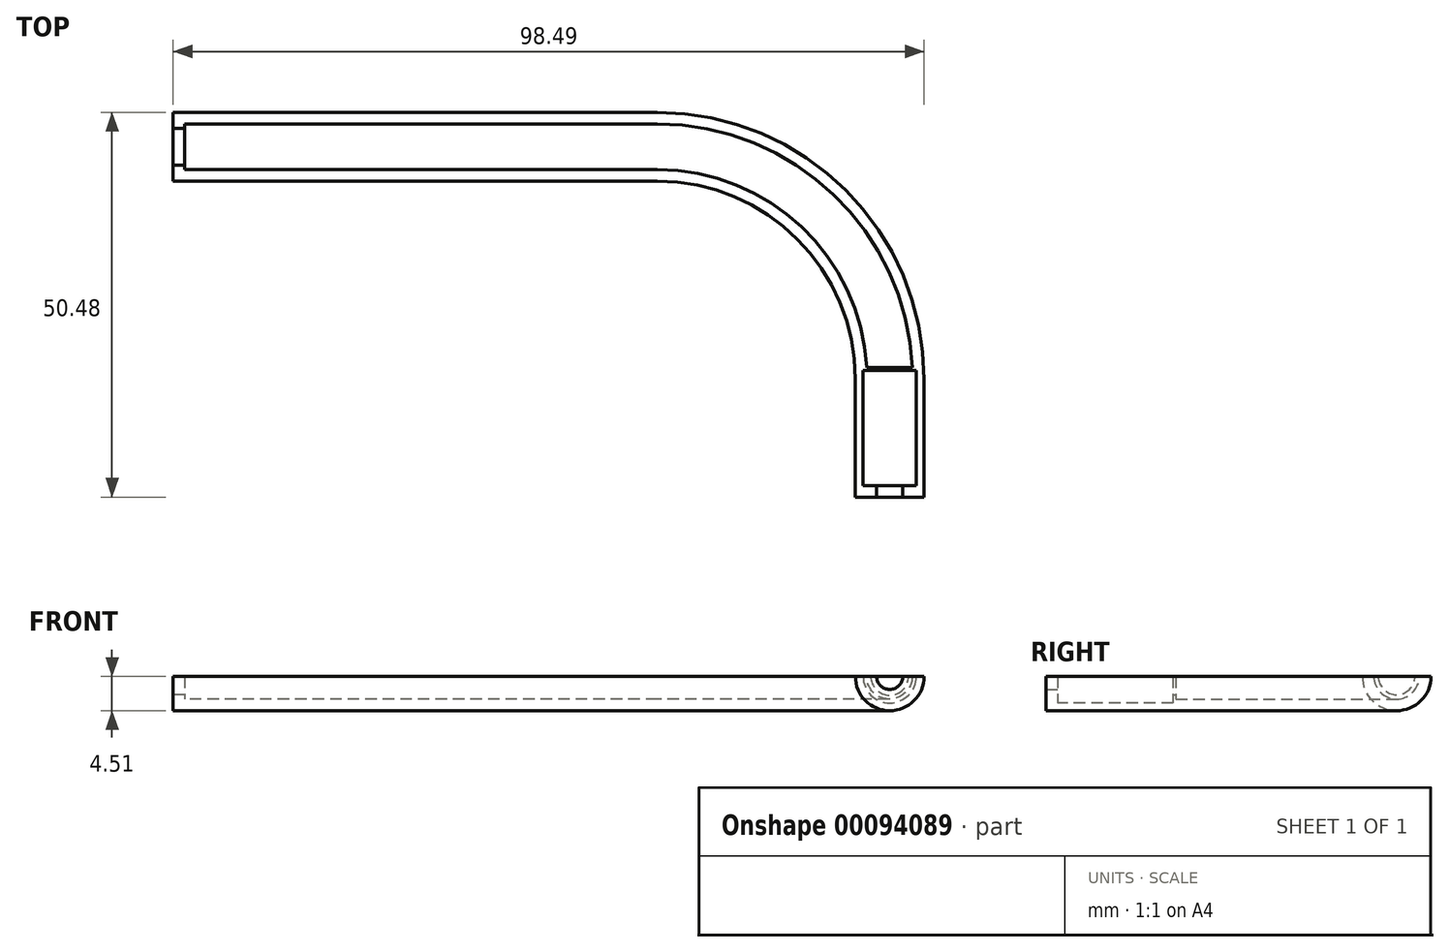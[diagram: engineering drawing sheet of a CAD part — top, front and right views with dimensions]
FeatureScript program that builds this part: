
annotation { "Feature Type Name" : "Feature", "Feature Type Description" : "" }
export const myFeature = defineFeature(function(context is Context, id is Id, definition is map)
    precondition{}
    {
        {
            var Q0;
            Q0=qCreatedBy(makeId("Top.planeOp"),FACE);
            var sketch = newSketch(context, id + "F0", { "sketchPlane" : qUnion([Q0])});
            skLineSegment(sketch, "E0", {"start": v(0, 0) * mm, "end": v(63.5, 0) * mm});
            skArc(sketch, "E1", {"start": v(93.98, -30.48) * mm, "mid": v(85.05, -8.93) * mm, "end": v(63.5, 0) * mm});
            skSolve(sketch);
        }
        {
            var Q0;
            Q0=sQuery(id+"F0.wireOp",VERTEX,"E1.start");
            var Q1;
            Q1=qCreatedBy(makeId("Front.planeOp"),FACE);
            cPlane(context, id + "F1", {"entities" : qUnion([Q0, Q1]), "cplaneType" : CPlaneType.PLANE_POINT, "offset" : 25.4 * mm, "width" : 152.4 * mm, "height" : 152.4 * mm});
        }
        {
            var Q0;
            Q0=qCreatedBy(id+"F1.planeOp",FACE);
            var sketch = newSketch(context, id + "F2", { "sketchPlane" : qUnion([Q0])});
            skArc(sketch, "E2", {"start": v(89.47, 0) * mm, "mid": v(93.98, -4.5) * mm, "end": v(98.49, 0) * mm});
            skLineSegment(sketch, "E3", {"start": v(89.47, 0) * mm, "end": v(98.49, 0) * mm});
            skSolve(sketch);
        }
        {
            var Q0;
            Q0=makeQuery(id+"F2.imprint","IMPRINT",FACE,{"disambiguationData":[TD([[makeQuery(id+"F2.imprint","IMPRINT",EDGE,{"derivedFrom":sQuery(id+"F2.wireOp",EDGE,"E2")}),1.0]])]});
            var Q1;
            Q1=sQuery(id+"F0.wireOp",EDGE,"E1");
            var Q2;
            Q2=sQuery(id+"F0.wireOp",EDGE,"E0");
            sweep(context, id + "F3", {"profiles" : qUnion([Q0]), "path" : qUnion([Q1, Q2])});
        }
        {
            var Q0;
            Q0=makeQuery(id+"F3.opSweep","SWEPT_FACE",FACE,{"disambiguationData":[OSD([sQuery(id+"F0.wireOp",EDGE,"E1"),sQuery(id+"F2.wireOp",EDGE,"E3")])]});
            shell(context, id + "F4", {"entities" : qUnion([Q0]), "thickness" : 1.52 * mm});
        }
        {
            var Q0;
            Q0=makeQuery(id+"F3.opSweep","CAP_FACE",FACE,{"disambiguationData":[OSD([sQuery(id+"F0.wireOp",VERTEX,"E1.start"),sQuery(id+"F2.wireOp",EDGE,"E2"),sQuery(id+"F2.wireOp",EDGE,"E3")])],"isStart":true});
            var sketch = newSketch(context, id + "F5", { "sketchPlane" : qUnion([Q0])});
            skCircle(sketch, "E4", {"center": v(93.98, 0) * mm, "radius": 2.48 * mm});
            skCircle(sketch, "E5", {"center": v(93.98, 0) * mm, "radius": 3.5 * mm});
            skSolve(sketch);
        }
        {
            var Q0;
            {var subQ0=sQuery(id+"F5.wireOp",EDGE,"E4");var subQ1=makeQuery(id+"F3.opSweep","CAP_EDGE",EDGE,{"disambiguationData":[OSD([sQuery(id+"F0.wireOp",VERTEX,"E1.start"),sQuery(id+"F2.wireOp",EDGE,"E3")])],"isStart":true});var subQ2=makeQuery(id+"F5.imprint","INTERSECT",VERTEX,{"disambiguationData":[OD(0.0)],"derivedFrom":[subQ1,subQ0]});Q0=makeQuery(id+"F5.imprint","IMPRINT",FACE,{"disambiguationData":[TD([[makeQuery(id+"F5.imprint","IMPRINT",EDGE,{"disambiguationData":[TD([[subQ2,-1.0]])],"derivedFrom":subQ0}),1.0]])]});}
            extrude(context, id + "F6", {"entities" : qUnion([Q0]), "operationType" : NewBodyOperationType.REMOVE, "endBound" : BoundingType.UP_TO_NEXT, "oppositeDirection" : true, "depth" : 25.4 * mm, "offsetDistance" : 25.4 * mm});
        }
        {
            var Q0;
            {var subQ0=sQuery(id+"F5.wireOp",EDGE,"E4");var subQ1=makeQuery(id+"F3.opSweep","CAP_EDGE",EDGE,{"disambiguationData":[OSD([sQuery(id+"F0.wireOp",VERTEX,"E1.start"),sQuery(id+"F2.wireOp",EDGE,"E3")])],"isStart":true});var subQ2=makeQuery(id+"F5.imprint","INTERSECT",VERTEX,{"disambiguationData":[OD(0.0)],"derivedFrom":[subQ1,subQ0]});Q0=makeQuery(id+"F5.imprint","IMPRINT",FACE,{"disambiguationData":[TD([[makeQuery(id+"F5.imprint","IMPRINT",EDGE,{"disambiguationData":[TD([[subQ2,-1.0]])],"derivedFrom":subQ0}),-1.0]])]});}
            extrude(context, id + "F7", {"entities" : qUnion([Q0]), "operationType" : NewBodyOperationType.REMOVE, "oppositeDirection" : true, "depth" : 1.14 * mm, "offsetDistance" : 25.4 * mm});
        }
        {
            var Q0;
            Q0=makeQuery(id+"F3.opSweep","CAP_FACE",FACE,{"disambiguationData":[OSD([sQuery(id+"F0.wireOp",VERTEX,"E0.start"),sQuery(id+"F2.wireOp",EDGE,"E2"),sQuery(id+"F2.wireOp",EDGE,"E3")])],"isStart":false});
            var sketch = newSketch(context, id + "F8", { "sketchPlane" : qUnion([Q0])});
            skCircle(sketch, "E6", {"center": v(0, 0) * mm, "radius": 2.41 * mm});
            skSolve(sketch);
        }
        {
            var Q0;
            {var subQ0=sQuery(id+"F8.wireOp",EDGE,"E6");var subQ1=makeQuery(id+"F3.opSweep","CAP_EDGE",EDGE,{"disambiguationData":[OSD([sQuery(id+"F0.wireOp",VERTEX,"E0.start"),sQuery(id+"F2.wireOp",EDGE,"E3")])],"isStart":false});var subQ2=makeQuery(id+"F8.imprint","INTERSECT",VERTEX,{"disambiguationData":[OD(0.0)],"derivedFrom":[subQ1,subQ0]});Q0=makeQuery(id+"F8.imprint","IMPRINT",FACE,{"disambiguationData":[TD([[makeQuery(id+"F8.imprint","IMPRINT",EDGE,{"disambiguationData":[TD([[subQ2,1.0]])],"derivedFrom":subQ0}),1.0]])]});}
            extrude(context, id + "F9", {"entities" : qUnion([Q0]), "operationType" : NewBodyOperationType.REMOVE, "endBound" : BoundingType.UP_TO_NEXT, "oppositeDirection" : true, "depth" : 25.4 * mm, "offsetDistance" : 25.4 * mm});
        }
        {
            var Q0;
            {var subQ1=sQuery(id+"F0.wireOp",VERTEX,"E1.start");var subQ5=makeQuery(id+"F3.opSweep","CAP_EDGE",EDGE,{"disambiguationData":[OSD([subQ1,sQuery(id+"F2.wireOp",EDGE,"E2")])],"isStart":true});Q0=makeQuery(id+"F5.imprint","IMPRINT",FACE,{"disambiguationData":[TD([[makeQuery(id+"F5.imprint","IMPRINT",EDGE,{"derivedFrom":subQ5}),-1.0]])]});}
            extrude(context, id + "F10", {"entities" : qUnion([Q0]), "operationType" : NewBodyOperationType.ADD, "depth" : 13.97 * mm, "offsetDistance" : 25.4 * mm});
        }
        {
            var Q0;
            Q0=makeQuery(id+"F10.opExtrude","CAP_FACE",FACE,{"disambiguationData":[OSD([sQuery(id+"F0.wireOp",VERTEX,"E1.start"),sQuery(id+"F2.wireOp",EDGE,"E2"),sQuery(id+"F2.wireOp",EDGE,"E3"),sQuery(id+"F5.wireOp",EDGE,"E5")])],"isStart":false});
            var sketch = newSketch(context, id + "F11", { "sketchPlane" : qUnion([Q0])});
            skArc(sketch, "E7.0.0", {"start": v(97.47, 0) * mm, "mid": v(93.98, -3.5) * mm, "end": v(90.49, 0) * mm});
            skLineSegment(sketch, "E7.0.1", {"start": v(90.49, 0) * mm, "end": v(89.47, 0) * mm});
            skArc(sketch, "E7.0.2", {"start": v(98.49, 0) * mm, "mid": v(93.98, -4.5) * mm, "end": v(89.47, 0) * mm});
            skLineSegment(sketch, "E7.0.3", {"start": v(98.49, 0) * mm, "end": v(97.47, 0) * mm});
            skCircle(sketch, "E8", {"center": v(93.98, 0) * mm, "radius": 1.71 * mm});
            skLineSegment(sketch, "E9", {"start": v(89.47, 0) * mm, "end": v(92.27, 0) * mm});
            skLineSegment(sketch, "E10", {"start": v(98.49, 0) * mm, "end": v(95.7, 0) * mm});
            skSolve(sketch);
        }
        {
            var Q0;
            {var subQ0=sQuery(id+"F11.wireOp",EDGE,"E7.0.0");Q0=makeQuery(id+"F11.imprint","IMPRINT",FACE,{"disambiguationData":[TD([[makeQuery(id+"F11.imprint","IMPRINT",EDGE,{"derivedFrom":subQ0}),1.0]])]});}
            var Q1;
            {var subQ0=sQuery(id+"F11.wireOp",EDGE,"E7.0.0");Q1=makeQuery(id+"F11.imprint","IMPRINT",FACE,{"disambiguationData":[TD([[makeQuery(id+"F11.imprint","IMPRINT",EDGE,{"derivedFrom":subQ0}),-1.0]])]});}
            extrude(context, id + "F12", {"entities" : qUnion([Q0, Q1]), "operationType" : NewBodyOperationType.ADD, "depth" : 1.52 * mm, "offsetDistance" : 25.4 * mm});
        }
    });
